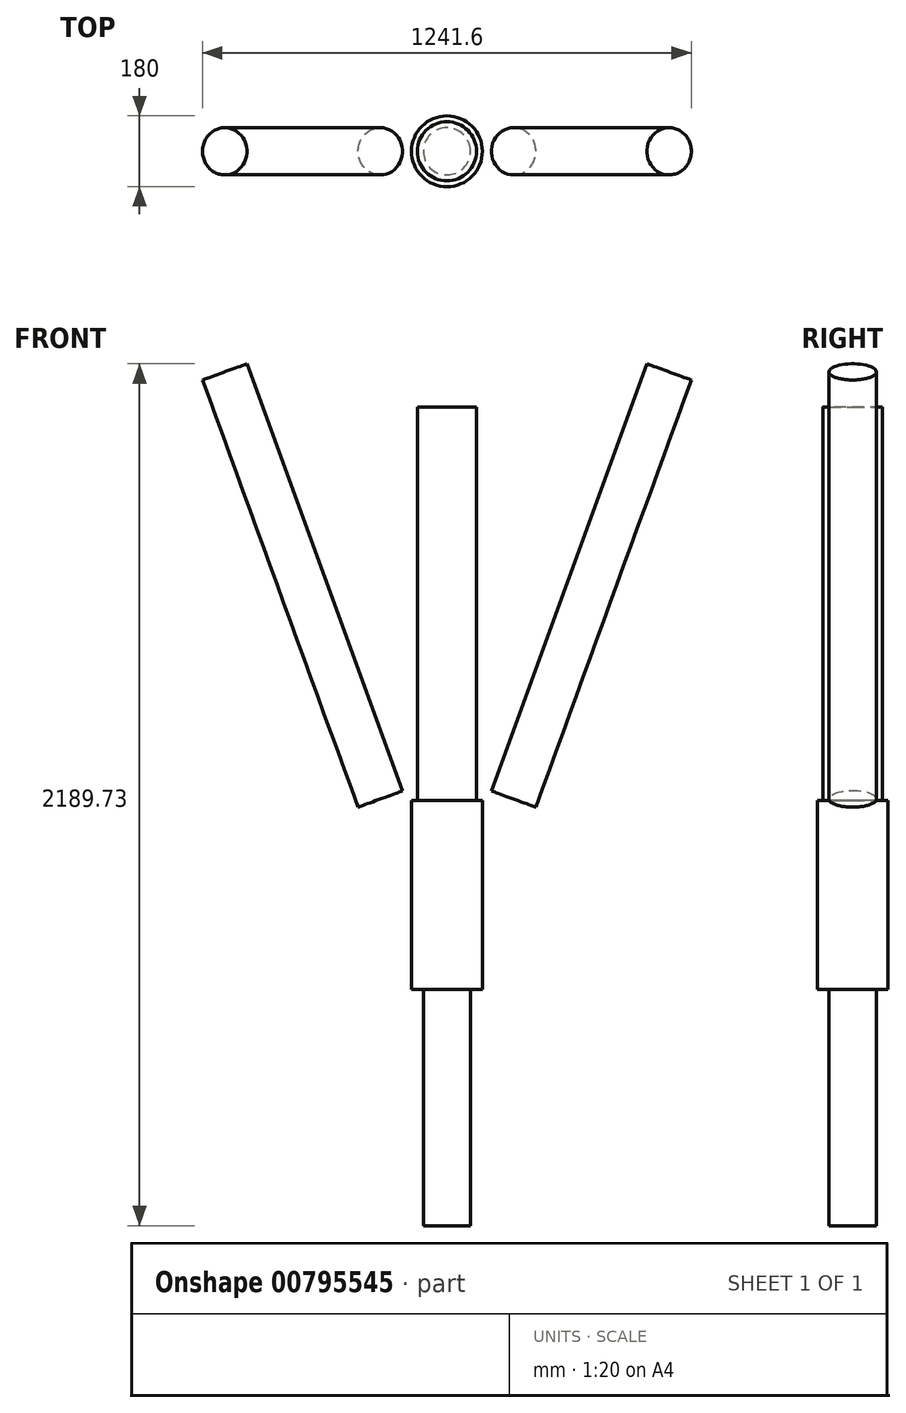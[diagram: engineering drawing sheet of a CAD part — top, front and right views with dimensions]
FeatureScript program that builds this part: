
annotation { "Feature Type Name" : "Feature", "Feature Type Description" : "" }
export const myFeature = defineFeature(function(context is Context, id is Id, definition is map)
    precondition{}
    {
        {
            var Q0;
            Q0=qCreatedBy(makeId("Top.planeOp"),FACE);
            var sketch = newSketch(context, id + "F0", { "sketchPlane" : qUnion([Q0])});
            skCircle(sketch, "E0", {"center": v(0, 0) * mm, "radius": 90 * mm});
            skCircle(sketch, "E1", {"center": v(0, 0) * mm, "radius": 75 * mm});
            skSolve(sketch);
        }
        {
            var Q0;
            Q0=makeQuery(id+"F0.imprint","IMPRINT",FACE,{"disambiguationData":[TD([[makeQuery(id+"F0.imprint","IMPRINT",EDGE,{"derivedFrom":sQuery(id+"F0.wireOp",EDGE,"E1")}),1.0]])]});
            extrude(context, id + "F1", {"entities" : qUnion([Q0]), "depth" : 1000 * mm, "offsetDistance" : 25 * mm});
        }
        {
            var Q0;
            Q0 = qSketchRegion(id + "F0", true);
            var Q1;
            Q1=makeQuery(id+"F0.imprint","IMPRINT",FACE,{"disambiguationData":[TD([[makeQuery(id+"F0.imprint","IMPRINT",EDGE,{"derivedFrom":sQuery(id+"F0.wireOp",EDGE,"E1")}),1.0]])]});
            extrude(context, id + "F2", {"entities" : qUnion([Q0, Q1]), "oppositeDirection" : true, "depth" : 480 * mm, "offsetDistance" : 25 * mm});
        }
        {
            var Q0;
            Q0=makeQuery(id+"F2.opExtrude","CAP_FACE",FACE,{"disambiguationData":[OSD([sQuery(id+"F0.wireOp",EDGE,"E0")])],"isStart":true});
            var sketch = newSketch(context, id + "F3", { "sketchPlane" : qUnion([Q0])});
            skLineSegment(sketch, "E2.bottom", {"start": v(180, 90) * mm, "end": v(-180, 90) * mm});
            skLineSegment(sketch, "E2.top", {"start": v(180, -90) * mm, "end": v(-180, -90) * mm});
            skLineSegment(sketch, "E2.left", {"start": v(180, 90) * mm, "end": v(180, -90) * mm});
            skLineSegment(sketch, "E2.right", {"start": v(-180, 90) * mm, "end": v(-180, -90) * mm});
            skPoint(sketch, "E2.middle", {"position": v(0, 0) * mm});
            skSolve(sketch);
        }
        {
            var Q0;
            Q0=sQuery(id+"F3.wireOp",EDGE,"E2.right");
            cPlane(context, id + "F4", {"entities" : qUnion([Q0]), "cplaneType" : CPlaneType.LINE_ANGLE, "offset" : 25 * mm, "angle" : 20 * degree, "width" : 150 * mm, "height" : 150 * mm});
        }
        {
            var Q0;
            Q0=qCreatedBy(id+"F4.planeOp",FACE);
            var sketch = newSketch(context, id + "F5", { "sketchPlane" : qUnion([Q0])});
            skCircle(sketch, "E3", {"center": v(-157.85, 0) * mm, "radius": 60 * mm});
            skSolve(sketch);
        }
        {
            var Q0;
            Q0=makeQuery(id+"F5.imprint","IMPRINT",FACE,{"disambiguationData":[TD([[makeQuery(id+"F5.imprint","IMPRINT",EDGE,{"derivedFrom":sQuery(id+"F5.wireOp",EDGE,"E3")}),1.0]])]});
            extrude(context, id + "F6", {"entities" : qUnion([Q0]), "oppositeDirection" : true, "depth" : 1155 * mm, "offsetDistance" : 25 * mm});
        }
        {
            var Q0;
            Q0=makeQuery(id+"F6.opExtrude","SWEPT_BODY",BODY,{"disambiguationData":[OSD([sQuery(id+"F5.wireOp",EDGE,"E3")])]});
            var Q1;
            Q1=qCreatedBy(makeId("Right.planeOp"),FACE);
            mirror(context, id + "F7", {"entities" : qUnion([Q0]), "mirrorPlane" : qUnion([Q1])});
        }
        {
            var Q0;
            Q0=makeQuery(id+"F2.opExtrude","CAP_FACE",FACE,{"disambiguationData":[OSD([sQuery(id+"F0.wireOp",EDGE,"E0")])],"isStart":false});
            var sketch = newSketch(context, id + "F8", { "sketchPlane" : qUnion([Q0])});
            skCircle(sketch, "E4", {"center": v(0, 0) * mm, "radius": 60 * mm});
            skSolve(sketch);
        }
        {
            var Q0;
            Q0 = qSketchRegion(id + "F8", true);
            extrude(context, id + "F9", {"entities" : qUnion([Q0]), "depth" : 600 * mm, "offsetDistance" : 25 * mm});
        }
    });
